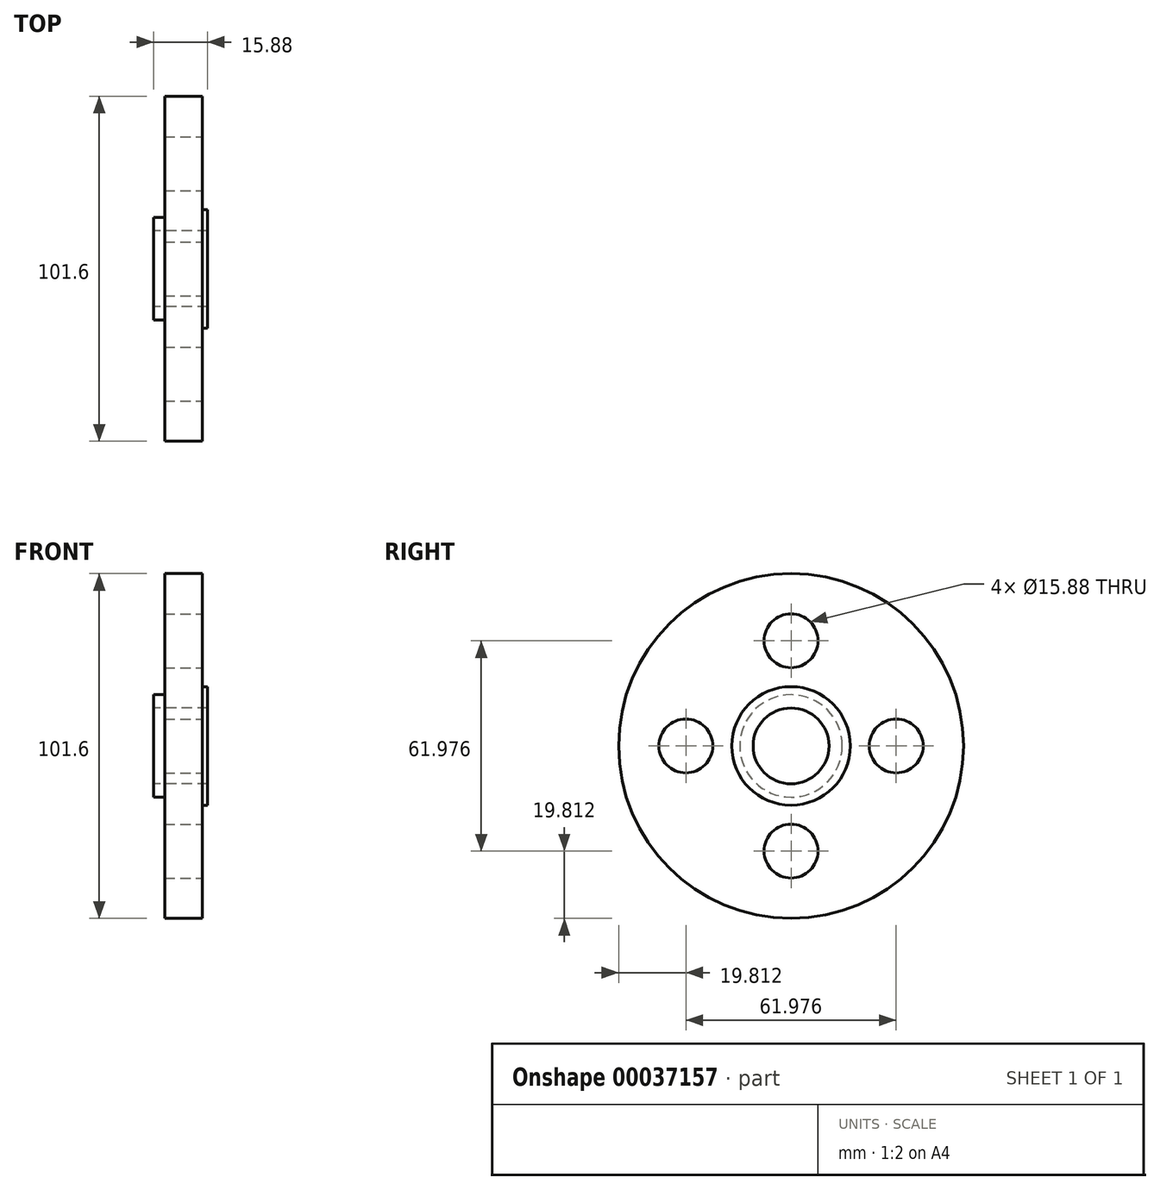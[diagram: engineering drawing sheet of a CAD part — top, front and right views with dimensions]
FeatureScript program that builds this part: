
annotation { "Feature Type Name" : "Feature", "Feature Type Description" : "" }
export const myFeature = defineFeature(function(context is Context, id is Id, definition is map)
    precondition{}
    {
        {
            var Q0;
            Q0=qCreatedBy(makeId("Front.planeOp"),FACE);
            var sketch = newSketch(context, id + "F0", { "sketchPlane" : qUnion([Q0])});
            skLineSegment(sketch, "E0", {"start": v(-68.76, 0) * mm, "end": v(67.91, 0) * mm, "construction": true});
            skLineSegment(sketch, "E1", {"start": v(0, 15.09) * mm, "end": v(3.25, 15.09) * mm});
            skLineSegment(sketch, "E2", {"start": v(3.25, 15.09) * mm, "end": v(3.25, 50.8) * mm});
            skLineSegment(sketch, "E3", {"start": v(3.25, 50.8) * mm, "end": v(14.35, 50.8) * mm});
            skLineSegment(sketch, "E4", {"start": v(14.35, 50.8) * mm, "end": v(14.35, 17.46) * mm});
            skLineSegment(sketch, "E5", {"start": v(14.35, 17.46) * mm, "end": v(15.87, 17.46) * mm});
            skLineSegment(sketch, "E6", {"start": v(15.88, 17.46) * mm, "end": v(15.88, 11.18) * mm});
            skLineSegment(sketch, "E7", {"start": v(15.88, 11.18) * mm, "end": v(0, 11.18) * mm});
            skLineSegment(sketch, "E8", {"start": v(0, 11.18) * mm, "end": v(0, 15.09) * mm});
            skSolve(sketch);
        }
        {
            var Q0;
            Q0 = qSketchRegion(id + "F0", true);
            var Q1;
            Q1=sQuery(id+"F0.wireOp",EDGE,"E0");
            revolve(context, id + "F1", {"entities" : qUnion([Q0]), "axis" : qUnion([Q1]), "revolveType" : RevolveType.FULL});
        }
        {
            var Q0;
            Q0=makeQuery(id+"F1.opRevolve","SWEPT_FACE",FACE,{"disambiguationData":[OSD([sQuery(id+"F0.wireOp",EDGE,"E4")])]});
            var sketch = newSketch(context, id + "F2", { "sketchPlane" : qUnion([Q0])});
            skCircle(sketch, "E9", {"center": v(0, 0) * mm, "radius": 30.99 * mm, "construction": true});
            skCircle(sketch, "E10", {"center": v(0, 30.99) * mm, "radius": 7.94 * mm});
            skCircle(sketch, "E11.1.0", {"center": v(-30.99, 0) * mm, "radius": 7.94 * mm});
            skCircle(sketch, "E11.2.0", {"center": v(0, -30.99) * mm, "radius": 7.94 * mm});
            skCircle(sketch, "E11.3.0", {"center": v(30.99, 0) * mm, "radius": 7.94 * mm});
            skSolve(sketch);
        }
        {
            var Q0;
            Q0 = qSketchRegion(id + "F2", true);
            extrude(context, id + "F3", {"entities" : qUnion([Q0]), "operationType" : NewBodyOperationType.REMOVE, "endBound" : BoundingType.THROUGH_ALL, "oppositeDirection" : true, "depth" : 25.4 * mm});
        }
    });
